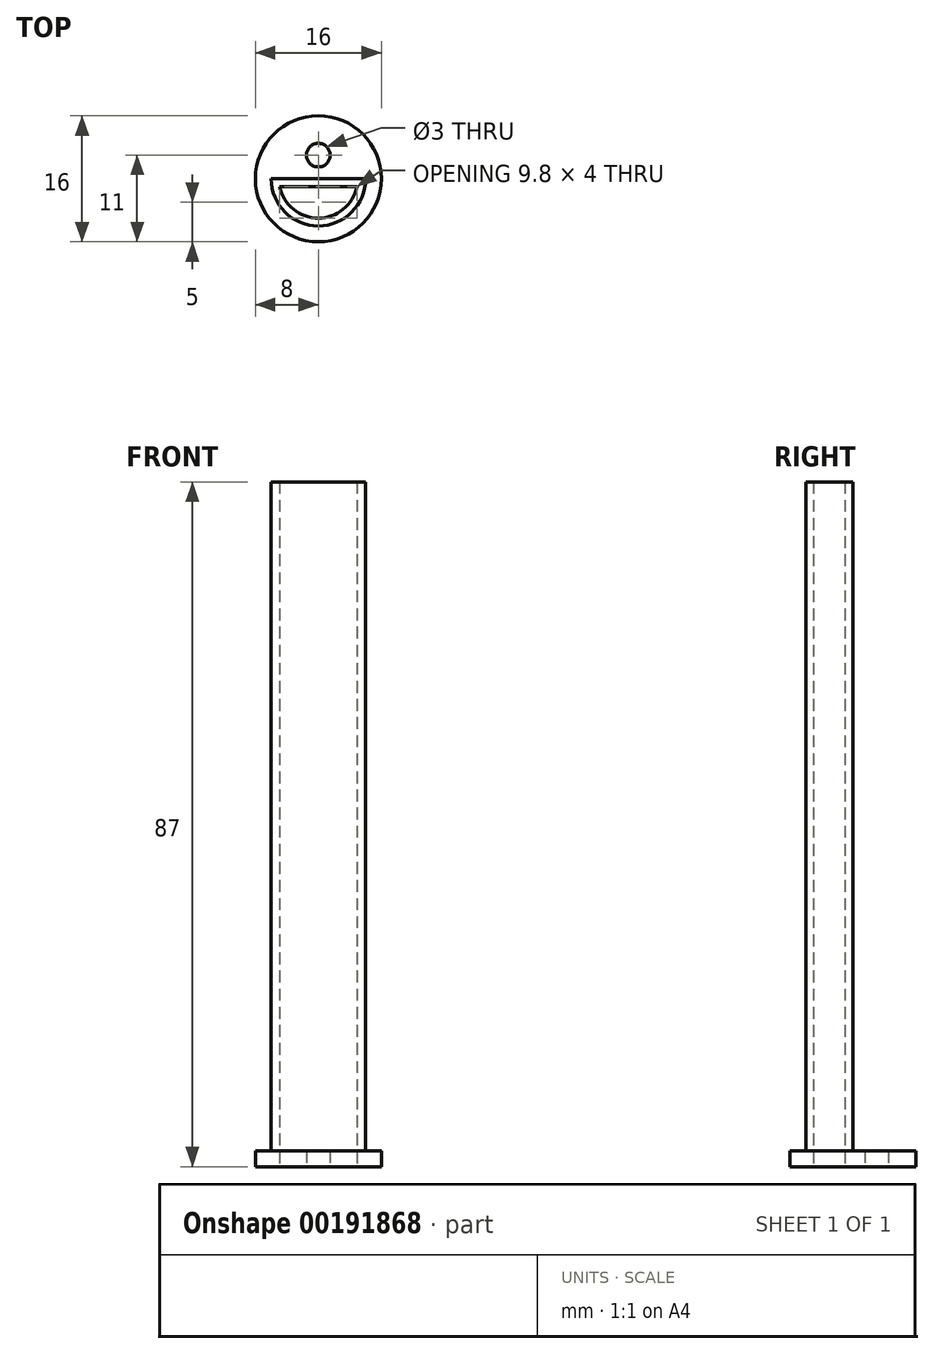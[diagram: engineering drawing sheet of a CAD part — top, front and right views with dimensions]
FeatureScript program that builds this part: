
annotation { "Feature Type Name" : "Feature", "Feature Type Description" : "" }
export const myFeature = defineFeature(function(context is Context, id is Id, definition is map)
    precondition{}
    {
        {
            var Q0;
            Q0=qCreatedBy(makeId("Top.planeOp"),FACE);
            var sketch = newSketch(context, id + "F0", { "sketchPlane" : qUnion([Q0])});
            skCircle(sketch, "E0", {"center": v(0, 0) * mm, "radius": 8 * mm});
            skArc(sketch, "E1", {"start": v(-6, 0) * mm, "mid": v(0, -6) * mm, "end": v(6, 0) * mm});
            skArc(sketch, "E2", {"start": v(-4.9, -1) * mm, "mid": v(0, -5) * mm, "end": v(4.9, -1) * mm});
            skLineSegment(sketch, "E3", {"start": v(-4.9, -1) * mm, "end": v(4.9, -1) * mm});
            skLineSegment(sketch, "E4", {"start": v(6, 0) * mm, "end": v(-6, 0) * mm});
            skSolve(sketch);
        }
        {
            var Q0;
            Q0=makeQuery(id+"F0.imprint","IMPRINT",FACE,{"disambiguationData":[TD([[makeQuery(id+"F0.imprint","IMPRINT",EDGE,{"derivedFrom":sQuery(id+"F0.wireOp",EDGE,"E1")}),1.0]])]});
            extrude(context, id + "F1", {"entities" : qUnion([Q0]), "depth" : 87 * mm});
        }
        {
            var Q0;
            Q0 = qSketchRegion(id + "F0", true);
            extrude(context, id + "F2", {"entities" : qUnion([Q0]), "operationType" : NewBodyOperationType.ADD, "depth" : 2 * mm});
        }
        {
            var Q0;
            {var subQ0=sQuery(id+"F0.wireOp",EDGE,"E4");var subQ1=sQuery(id+"F0.wireOp",EDGE,"E1");Q0=makeQuery(id+"F2.boolean.opBoolean","MERGE",FACE,{"derivedFrom":[makeQuery(id+"F1.opExtrude","CAP_FACE",FACE,{"disambiguationData":[OSD([subQ1,sQuery(id+"F0.wireOp",EDGE,"E2"),sQuery(id+"F0.wireOp",EDGE,"E3"),subQ0])],"isStart":true}),makeQuery(id+"F2.opExtrude","CAP_FACE",FACE,{"disambiguationData":[OSD([sQuery(id+"F0.wireOp",EDGE,"E0"),subQ1,subQ0])],"isStart":true})]});}
            var sketch = newSketch(context, id + "F3", { "sketchPlane" : qUnion([Q0])});
            skCircle(sketch, "E5", {"center": v(0, -3) * mm, "radius": 1.5 * mm});
            skSolve(sketch);
        }
        {
            var Q0;
            Q0=makeQuery(id+"F3.imprint","IMPRINT",FACE,{"disambiguationData":[TD([[makeQuery(id+"F3.imprint","IMPRINT",EDGE,{"derivedFrom":sQuery(id+"F3.wireOp",EDGE,"E5")}),1.0]])]});
            extrude(context, id + "F4", {"entities" : qUnion([Q0]), "operationType" : NewBodyOperationType.REMOVE, "oppositeDirection" : true, "depth" : 25 * mm});
        }
    });
